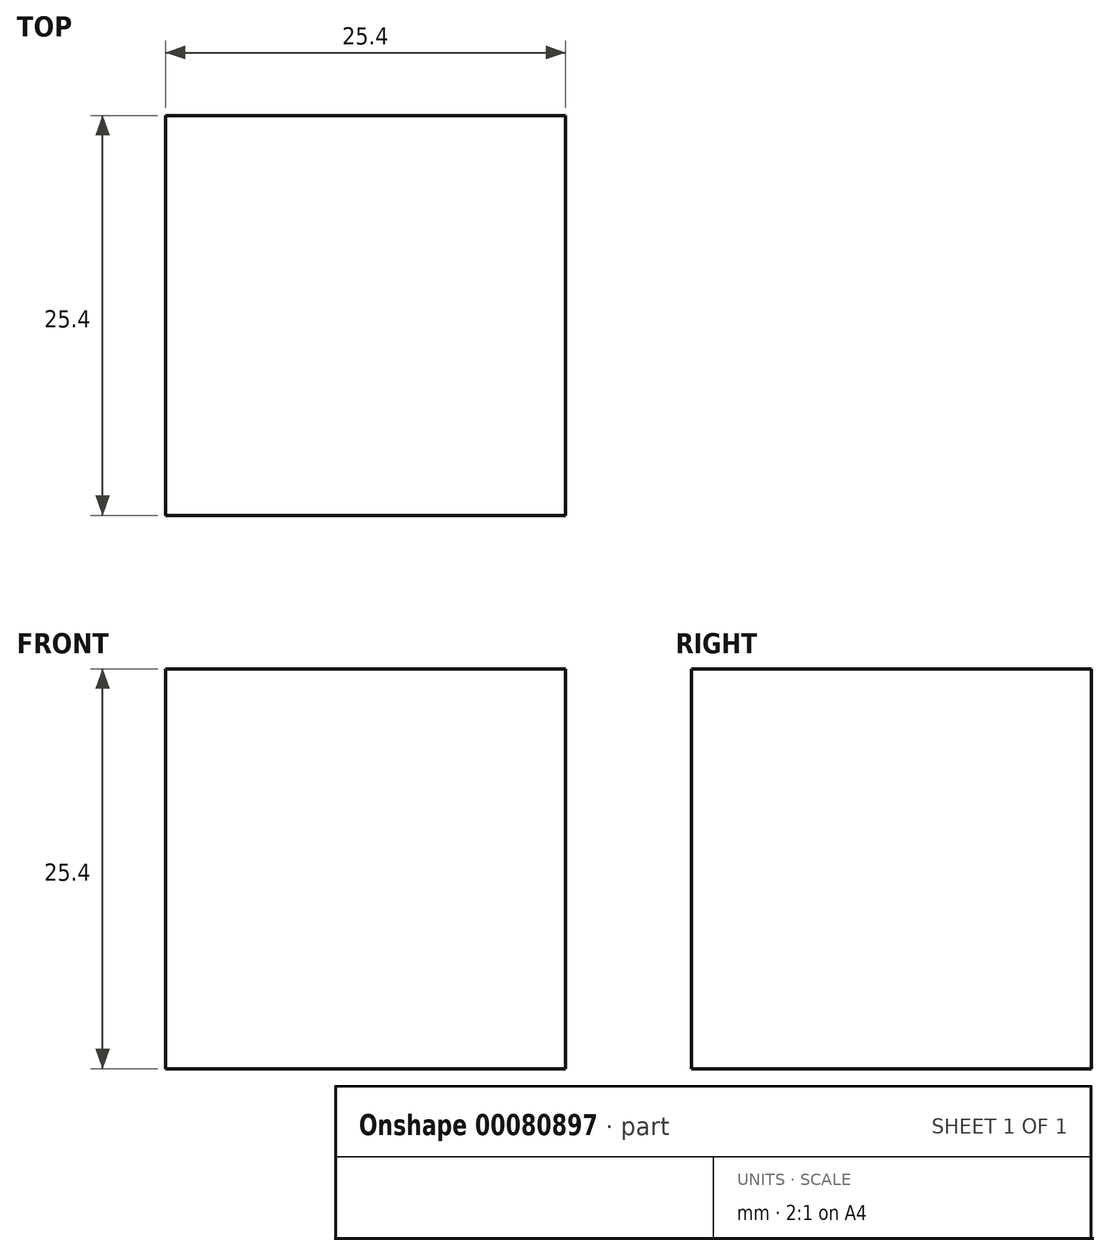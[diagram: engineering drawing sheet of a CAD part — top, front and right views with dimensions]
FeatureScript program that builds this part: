
annotation { "Feature Type Name" : "Feature", "Feature Type Description" : "" }
export const myFeature = defineFeature(function(context is Context, id is Id, definition is map)
    precondition{}
    {
        {
            var Q0;
            Q0=qCreatedBy(makeId("Top.planeOp"),FACE);
            var sketch = newSketch(context, id + "F0", { "sketchPlane" : qUnion([Q0])});
            skLineSegment(sketch, "E0.bottom", {"start": v(12.7, -12.7) * mm, "end": v(-12.7, -12.7) * mm});
            skLineSegment(sketch, "E0.top", {"start": v(12.7, 12.7) * mm, "end": v(-12.7, 12.7) * mm});
            skLineSegment(sketch, "E0.left", {"start": v(12.7, -12.7) * mm, "end": v(12.7, 12.7) * mm});
            skLineSegment(sketch, "E0.right", {"start": v(-12.7, -12.7) * mm, "end": v(-12.7, 12.7) * mm});
            skPoint(sketch, "E0.middle", {"position": v(0, 0) * mm});
            skSolve(sketch);
        }
        {
            var Q0;
            Q0 = qSketchRegion(id + "F0", true);
            extrude(context, id + "F1", {"entities" : qUnion([Q0]), "depth" : 25.4 * mm});
        }
    });
